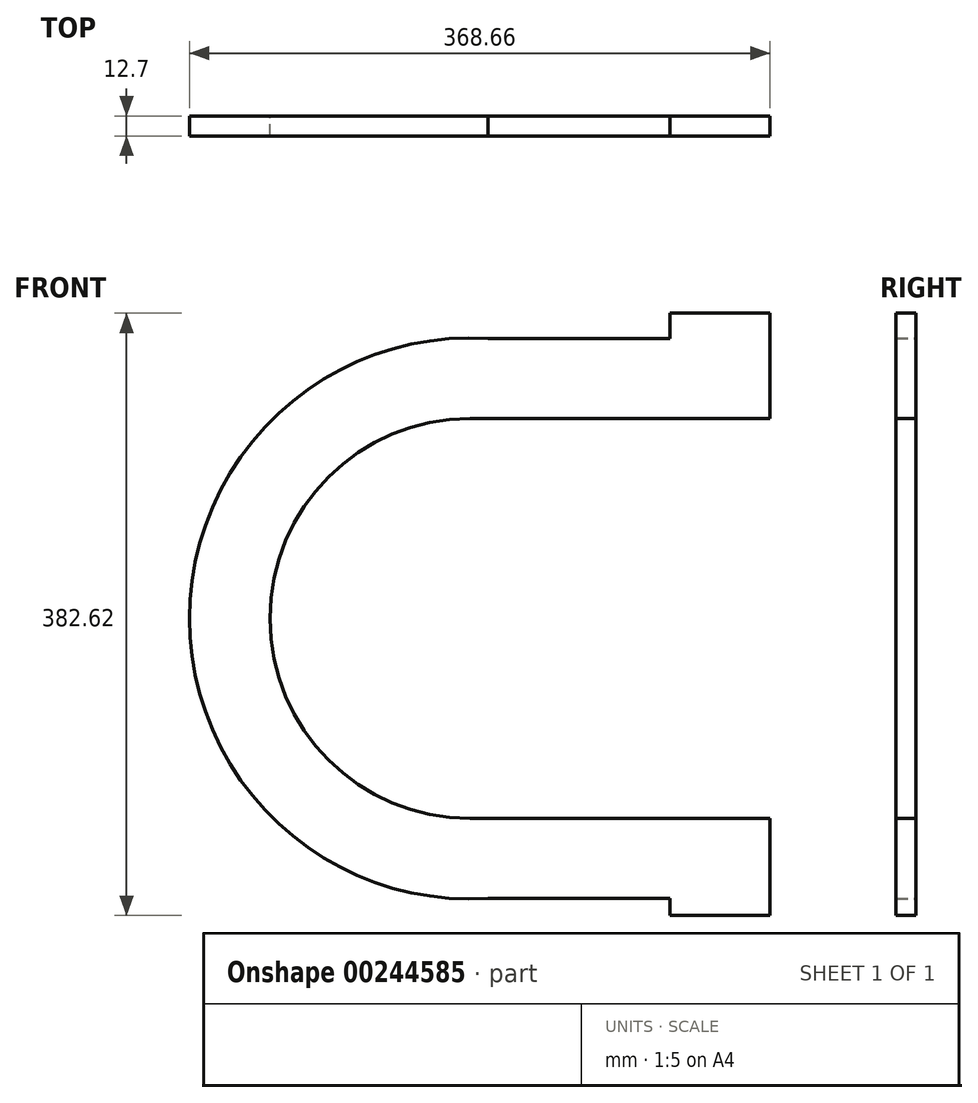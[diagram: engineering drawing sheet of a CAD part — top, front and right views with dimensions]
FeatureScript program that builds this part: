
annotation { "Feature Type Name" : "Feature", "Feature Type Description" : "" }
export const myFeature = defineFeature(function(context is Context, id is Id, definition is map)
    precondition{}
    {
        {
            var Q0;
            Q0=qCreatedBy(makeId("Front.planeOp"),FACE);
            var sketch = newSketch(context, id + "F0", { "sketchPlane" : qUnion([Q0])});
            skLineSegment(sketch, "E0.bottom", {"start": v(-11.3, -177.8) * mm, "end": v(127, -177.8) * mm});
            skLineSegment(sketch, "E0.top", {"start": v(-11.3, 177.8) * mm, "end": v(127, 177.8) * mm});
            skLineSegment(sketch, "E0.right", {"start": v(190.5, -177.8) * mm, "end": v(190.5, -127) * mm});
            skPoint(sketch, "E0.middle", {"position": v(0, 0) * mm});
            skArc(sketch, "E1", {"start": v(0, 127) * mm, "mid": v(-127, 0) * mm, "end": v(0, -127) * mm});
            skArc(sketch, "E2", {"start": v(11.3, 177.8) * mm, "mid": v(-178.16, 0) * mm, "end": v(11.3, -177.8) * mm});
            skLineSegment(sketch, "E3", {"start": v(0, 127) * mm, "end": v(190.5, 127) * mm});
            skLineSegment(sketch, "E4", {"start": v(0, -127) * mm, "end": v(190.5, -127) * mm});
            skLineSegment(sketch, "E5.trimOffspring", {"start": v(190.5, 127) * mm, "end": v(190.5, 177.8) * mm});
            skPoint(sketch, "E6.orphan", {"position": v(-190.5, 177.8) * mm});
            skPoint(sketch, "E7.orphan", {"position": v(-190.5, -177.8) * mm});
            skLineSegment(sketch, "E8.bottom", {"start": v(190.5, 127) * mm, "end": v(127, 127) * mm});
            skLineSegment(sketch, "E8.top", {"start": v(190.5, 193.98) * mm, "end": v(127, 193.98) * mm});
            skLineSegment(sketch, "E8.left", {"start": v(190.5, 127) * mm, "end": v(190.5, 193.98) * mm});
            skLineSegment(sketch, "E8.right", {"start": v(127, 177.8) * mm, "end": v(127, 193.98) * mm});
            skLineSegment(sketch, "E9.bottom", {"start": v(190.5, -127) * mm, "end": v(127, -127) * mm});
            skLineSegment(sketch, "E9.top", {"start": v(190.5, -188.64) * mm, "end": v(127, -188.64) * mm});
            skLineSegment(sketch, "E9.left", {"start": v(190.5, -127) * mm, "end": v(190.5, -188.64) * mm});
            skLineSegment(sketch, "E9.right", {"start": v(127, -177.8) * mm, "end": v(127, -188.64) * mm});
            skSolve(sketch);
        }
        {
            var Q0;
            Q0 = qSketchRegion(id + "F0", true);
            extrude(context, id + "F1", {"entities" : qUnion([Q0]), "depth" : 12.7 * mm});
        }
    });
